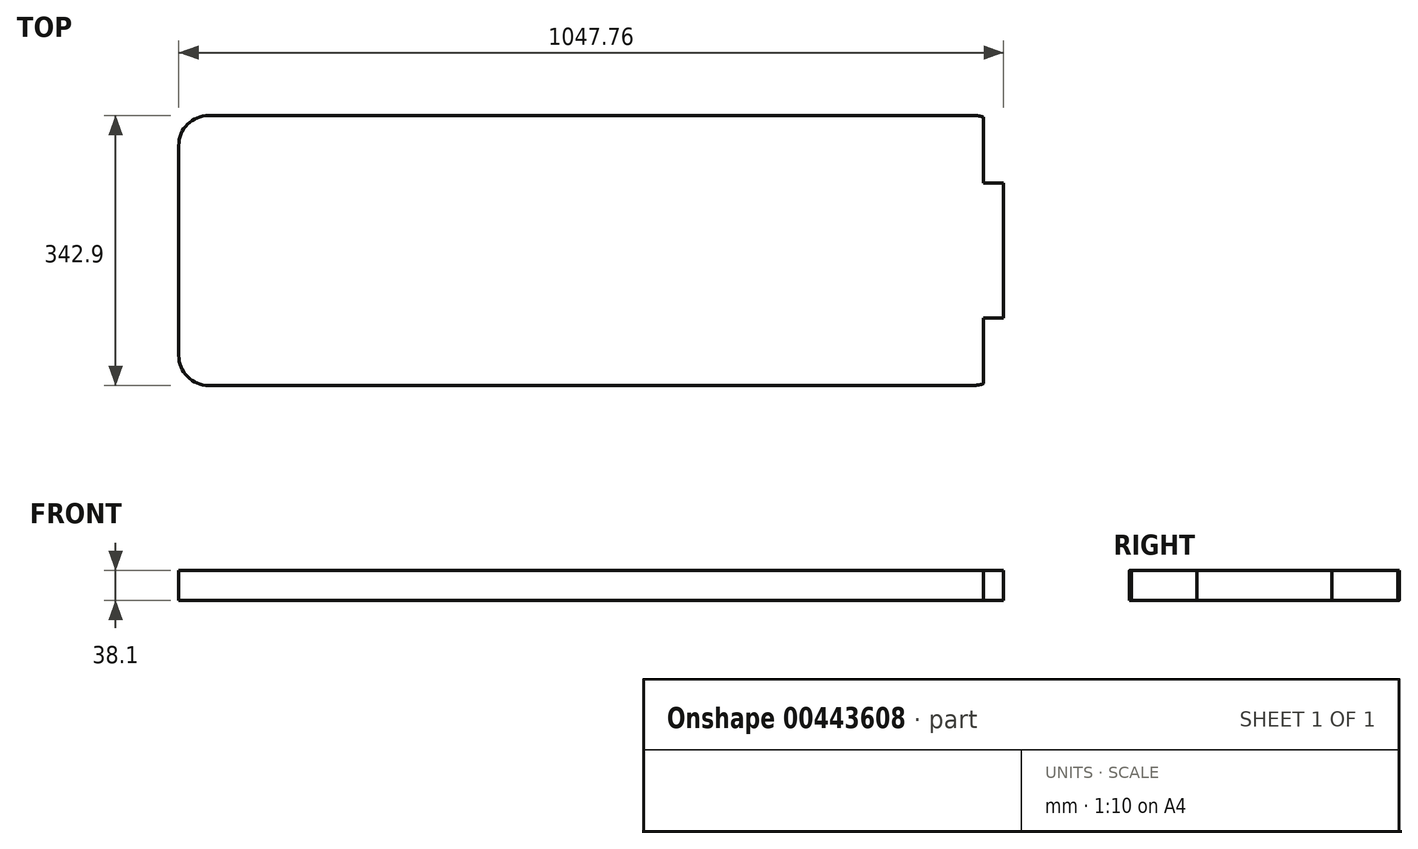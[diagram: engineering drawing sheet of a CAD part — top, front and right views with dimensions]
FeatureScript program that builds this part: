
annotation { "Feature Type Name" : "Feature", "Feature Type Description" : "" }
export const myFeature = defineFeature(function(context is Context, id is Id, definition is map)
    precondition{}
    {
        {
            var Q0;
            Q0=qCreatedBy(makeId("Top.planeOp"),FACE);
            var sketch = newSketch(context, id + "F0", { "sketchPlane" : qUnion([Q0])});
            skLineSegment(sketch, "E0.bottom", {"start": v(523.88, -171.45) * mm, "end": v(-523.88, -171.45) * mm});
            skLineSegment(sketch, "E0.top", {"start": v(523.88, 171.45) * mm, "end": v(-523.88, 171.45) * mm});
            skLineSegment(sketch, "E0.left", {"start": v(523.88, -171.45) * mm, "end": v(523.88, 171.45) * mm});
            skLineSegment(sketch, "E0.right", {"start": v(-523.88, -171.45) * mm, "end": v(-523.88, 171.45) * mm});
            skPoint(sketch, "E0.middle", {"position": v(0, 0) * mm});
            skSolve(sketch);
        }
        {
            var Q0;
            Q0=qSketchRegion(id+"F0",true);
            extrude(context, id + "F1", {"entities" : qUnion([Q0]), "depth" : 38.1 * mm});
        }
        {
            var Q0;
            Q0=makeQuery(id+"F1.opExtrude","SWEPT_EDGE",EDGE,{"disambiguationData":[OSD([sQuery(id+"F0.wireOp",EDGE,"E0.top"),sQuery(id+"F0.wireOp",EDGE,"E0.right")])]});
            var Q1;
            Q1=makeQuery(id+"F1.opExtrude","SWEPT_EDGE",EDGE,{"disambiguationData":[OSD([sQuery(id+"F0.wireOp",EDGE,"E0.bottom"),sQuery(id+"F0.wireOp",EDGE,"E0.right")])]});
            var Q2;
            Q2=makeQuery(id+"F1.opExtrude","SWEPT_EDGE",EDGE,{"disambiguationData":[OSD([sQuery(id+"F0.wireOp",EDGE,"E0.top"),sQuery(id+"F0.wireOp",EDGE,"E0.left")])]});
            var Q3;
            Q3=makeQuery(id+"F1.opExtrude","SWEPT_EDGE",EDGE,{"disambiguationData":[OSD([sQuery(id+"F0.wireOp",EDGE,"E0.bottom"),sQuery(id+"F0.wireOp",EDGE,"E0.left")])]});
            fillet(context, id + "F2", {"entities" : qUnion([Q0, Q1, Q2, Q3]), "radius" : 38.1 * mm, "tangentPropagation" : true, "allowEdgeOverflow" : false});
        }
        {
            var Q0;
            Q0=makeQuery(id+"F1.opExtrude","CAP_FACE",FACE,{"disambiguationData":[OSD([sQuery(id+"F0.wireOp",EDGE,"E0.bottom"),sQuery(id+"F0.wireOp",EDGE,"E0.top"),sQuery(id+"F0.wireOp",EDGE,"E0.left"),sQuery(id+"F0.wireOp",EDGE,"E0.right")])],"isStart":false});
            var sketch = newSketch(context, id + "F3", { "sketchPlane" : qUnion([Q0])});
            skLineSegment(sketch, "E1", {"start": v(498.48, 171.45) * mm, "end": v(498.48, 85.73) * mm});
            skLineSegment(sketch, "E2", {"start": v(498.48, 85.73) * mm, "end": v(523.88, 85.73) * mm});
            skLineSegment(sketch, "E3", {"start": v(498.48, -171.45) * mm, "end": v(498.48, -85.72) * mm});
            skLineSegment(sketch, "E4", {"start": v(498.48, -85.72) * mm, "end": v(523.88, -85.72) * mm});
            skLineSegment(sketch, "E5", {"start": v(523.88, -85.72) * mm, "end": v(523.88, -171.45) * mm});
            skLineSegment(sketch, "E6", {"start": v(523.88, -171.45) * mm, "end": v(498.48, -171.45) * mm});
            skLineSegment(sketch, "E7", {"start": v(498.48, 171.45) * mm, "end": v(523.88, 171.45) * mm});
            skLineSegment(sketch, "E8", {"start": v(523.88, 171.45) * mm, "end": v(523.88, 85.73) * mm});
            skSolve(sketch);
        }
        {
            var Q0;
            Q0 = qSketchRegion(id + "F3", true);
            extrude(context, id + "F4", {"entities" : qUnion([Q0]), "operationType" : NewBodyOperationType.REMOVE, "oppositeDirection" : true, "depth" : 50.8 * mm});
        }
    });
